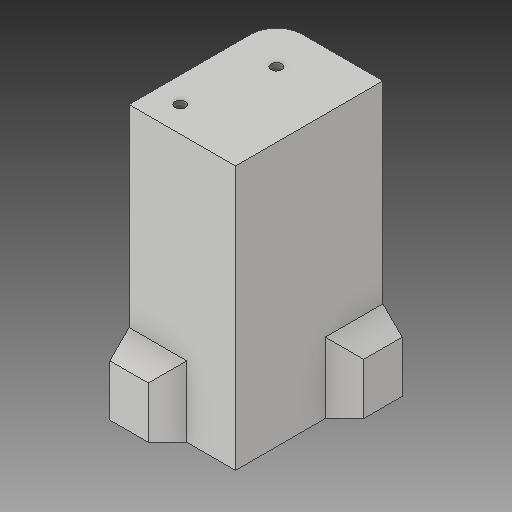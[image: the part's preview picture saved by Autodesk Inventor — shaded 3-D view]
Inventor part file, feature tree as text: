
AUTODESK INVENTOR PART (.ipt)
format: ipt  version: 2019 (Build 230136000, 136)  size: 189,952 bytes
history: native  units: in
note: dims shown in document units (in); Inventor stores cm internally (conversion verified against a paired STEP export)
features: sketch x6, projected_geometry x5, extrude x4, fillet x2, hole x2, chamfer x1
ambient origin geometry x8: Origin, YZ Plane, XZ Plane, XY Plane, X Axis, Y Axis, Z Axis, Center Point
bodies: Solid1 (feature_tree)
feature tree (20):
  extrude  "Extrusion1"  Depth=0.636in
  extrude  "Extrusion3"  Depth=1.4375in
  extrude  "Extrusion4"  Depth=0.1875in TaperAngle=0.0deg
  fillet  "Fillet1"  Radius=1.25in
  extrude  "Extrusion5"  Depth=0.85in TaperAngle=0.0deg
  chamfer  "Chamfer1"  Distance=0.375in
  hole  "Hole1"  [1 undecoded]
  hole  "Hole2"  [1 undecoded]
  fillet  "Fillet2"  Radius=0.5in
  sketch  "Sketch1"  dims[d0=2.57in d1=0.636in]
  sketch  "Sketch3"  dims[d4=0.1875in d5=0.0in d11=1.4375in]
  projected_geometry  "Projected Loop2"
  sketch  "Sketch4"  dims[d12=1.0375in d13=0.1875in d14=0.0in d15=1.25in]
  projected_geometry  "Projected Loop3"
  sketch  "Sketch6"  dims[d16=0.85in d17=0.1875in d18=0.0in]
  projected_geometry  "Projected Loop5"
  sketch  "Sketch8"  dims[d19=0.0625in]
  projected_geometry  "Projected Loop6"
  sketch  "Sketch9"  dims[d24=0.375in d25=0.375in d26=0.375in d27=0.375in d28=0.5in d29=0.0in d30=0.1875in d31=0.125in d32=45.0deg d33=0.104in d34=0.276in d35=0.375in d36=0.25in d37=0.5635in d38=0.5in d39=0.8108in d41=0.104in d42=0.276in d43=0.375in d44=0.25in d45=0.5635in d46=0.432in d47=0.8108in d50=1.25in d51=0.85in d52=0.25in d56=0.4in d57=0.25in d58=0.4in d59=0.25in]
  projected_geometry  "Projected Loop7"
note: 2 required parameter values undecoded (feature->parameter linkage not recoverable at this tier; creation-order binding heuristic only, values carry confidence <= 0.55)
